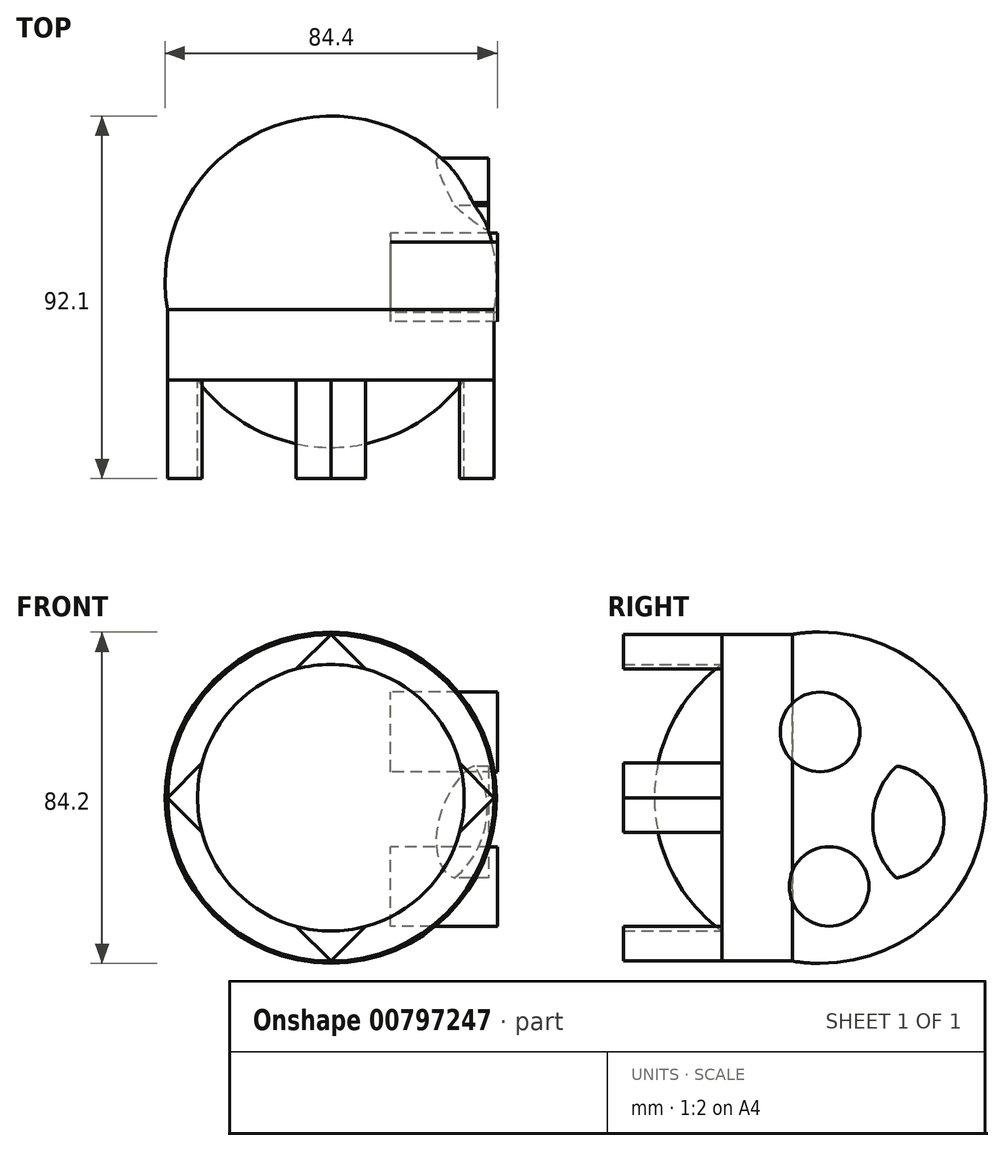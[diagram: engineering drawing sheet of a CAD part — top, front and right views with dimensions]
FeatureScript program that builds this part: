
annotation { "Feature Type Name" : "Feature", "Feature Type Description" : "" }
export const myFeature = defineFeature(function(context is Context, id is Id, definition is map)
    precondition{}
    {
        {
            var Q0;
            Q0=qCreatedBy(makeId("Front.planeOp"),FACE);
            var sketch = newSketch(context, id + "F0", { "sketchPlane" : qUnion([Q0])});
            skArc(sketch, "E0", {"start": v(0, 42.1) * mm, "mid": v(-42.1, 0) * mm, "end": v(0, -42.1) * mm});
            skLineSegment(sketch, "E1", {"start": v(0, 42.1) * mm, "end": v(0, -42.1) * mm});
            skSolve(sketch);
        }
        {
            var Q0;
            Q0 = qSketchRegion(id + "F0", true);
            var Q1;
            Q1=sQuery(id+"F0.wireOp",EDGE,"E1");
            revolve(context, id + "F1", {"surfaceOperationType" : NewSurfaceOperationType.NEW, "entities" : qUnion([Q0]), "axis" : qUnion([Q1]), "revolveType" : RevolveType.FULL});
        }
        {
            var Q0;
            Q0=qCreatedBy(makeId("Front.planeOp"),FACE);
            var sketch = newSketch(context, id + "F2", { "sketchPlane" : qUnion([Q0])});
            skCircle(sketch, "E2", {"center": v(0, 0) * mm, "radius": 41.5 * mm});
            skSolve(sketch);
        }
        {
            var Q0;
            Q0 = qSketchRegion(id + "F2", true);
            extrude(context, id + "F3", {"entities" : qUnion([Q0]), "operationType" : NewBodyOperationType.ADD, "depth" : 25 * mm, "offsetDistance" : 25 * mm});
        }
        {
            var Q0;
            Q0=makeQuery(id+"F3.opExtrude","CAP_FACE",FACE,{"disambiguationData":[OSD([sQuery(id+"F2.wireOp",EDGE,"E2")])],"isStart":false});
            var sketch = newSketch(context, id + "F4", { "sketchPlane" : qUnion([Q0])});
            skLineSegment(sketch, "E3", {"start": v(41.5, 0) * mm, "end": v(-41.5, 0) * mm});
            skLineSegment(sketch, "E4", {"start": v(-41.5, 0) * mm, "end": v(0, 41.5) * mm});
            skLineSegment(sketch, "E5", {"start": v(0, 41.5) * mm, "end": v(41.5, 0) * mm});
            skLineSegment(sketch, "E6", {"start": v(41.5, 0) * mm, "end": v(0, -41.5) * mm});
            skLineSegment(sketch, "E7", {"start": v(0, -41.5) * mm, "end": v(-41.5, 0) * mm});
            skSolve(sketch);
        }
        {
            var Q0;
            {var subQ0=sQuery(id+"F4.wireOp",EDGE,"E5");var subQ1=sQuery(id+"F4.wireOp",EDGE,"E4");var subQ2=sQuery(id+"F2.wireOp",EDGE,"E2");var subQ3=makeQuery(id+"F4.imprint","INTERSECT",VERTEX,{"derivedFrom":[makeQuery(id+"F3.opExtrude","CAP_EDGE",EDGE,{"disambiguationData":[OSD([subQ2])],"isStart":false}),subQ1,subQ0]});Q0=makeQuery(id+"F4.imprint","IMPRINT",FACE,{"disambiguationData":[TD([[makeQuery(id+"F4.imprint","IMPRINT",EDGE,{"disambiguationData":[TD([[subQ3,1.0]])],"derivedFrom":subQ1}),-1.0]])]});}
            var Q1;
            {var subQ1=sQuery(id+"F4.wireOp",EDGE,"E3");var subQ2=sQuery(id+"F2.wireOp",EDGE,"E2");var subQ4=makeQuery(id+"F3.boolean.opBoolean","INTERSECT",EDGE,{"derivedFrom":[makeQuery(id+"F1.opRevolve","SWEPT_FACE",FACE,{"disambiguationData":[OSD([sQuery(id+"F0.wireOp",EDGE,"E0")])]}),makeQuery(id+"F3.opExtrude","CAP_FACE",FACE,{"disambiguationData":[OSD([subQ2])],"isStart":false})]});var subQ5=makeQuery(id+"F4.imprint","INTERSECT",VERTEX,{"disambiguationData":[OD(0.0)],"derivedFrom":[subQ4,subQ1]});Q1=makeQuery(id+"F4.imprint","IMPRINT",FACE,{"disambiguationData":[TD([[makeQuery(id+"F4.imprint","IMPRINT",EDGE,{"disambiguationData":[TD([[subQ5,1.0]])],"derivedFrom":subQ1}),-1.0]])]});}
            var Q2;
            {var subQ1=sQuery(id+"F4.wireOp",EDGE,"E3");var subQ2=sQuery(id+"F2.wireOp",EDGE,"E2");var subQ4=makeQuery(id+"F3.boolean.opBoolean","INTERSECT",EDGE,{"derivedFrom":[makeQuery(id+"F1.opRevolve","SWEPT_FACE",FACE,{"disambiguationData":[OSD([sQuery(id+"F0.wireOp",EDGE,"E0")])]}),makeQuery(id+"F3.opExtrude","CAP_FACE",FACE,{"disambiguationData":[OSD([subQ2])],"isStart":false})]});var subQ5=makeQuery(id+"F4.imprint","INTERSECT",VERTEX,{"disambiguationData":[OD(0.0)],"derivedFrom":[subQ4,subQ1]});Q2=makeQuery(id+"F4.imprint","IMPRINT",FACE,{"disambiguationData":[TD([[makeQuery(id+"F4.imprint","IMPRINT",EDGE,{"disambiguationData":[TD([[subQ5,1.0]])],"derivedFrom":subQ1}),1.0]])]});}
            var Q3;
            {var subQ0=sQuery(id+"F4.wireOp",EDGE,"E7");var subQ1=sQuery(id+"F4.wireOp",EDGE,"E6");var subQ2=sQuery(id+"F2.wireOp",EDGE,"E2");var subQ3=makeQuery(id+"F4.imprint","INTERSECT",VERTEX,{"derivedFrom":[makeQuery(id+"F3.opExtrude","CAP_EDGE",EDGE,{"disambiguationData":[OSD([subQ2])],"isStart":false}),subQ1,subQ0]});Q3=makeQuery(id+"F4.imprint","IMPRINT",FACE,{"disambiguationData":[TD([[makeQuery(id+"F4.imprint","IMPRINT",EDGE,{"disambiguationData":[TD([[subQ3,1.0]])],"derivedFrom":subQ1}),-1.0]])]});}
            var Q4;
            {var subQ1=sQuery(id+"F4.wireOp",EDGE,"E3");var subQ2=sQuery(id+"F2.wireOp",EDGE,"E2");var subQ4=makeQuery(id+"F3.boolean.opBoolean","INTERSECT",EDGE,{"derivedFrom":[makeQuery(id+"F1.opRevolve","SWEPT_FACE",FACE,{"disambiguationData":[OSD([sQuery(id+"F0.wireOp",EDGE,"E0")])]}),makeQuery(id+"F3.opExtrude","CAP_FACE",FACE,{"disambiguationData":[OSD([subQ2])],"isStart":false})]});var subQ5=makeQuery(id+"F4.imprint","INTERSECT",VERTEX,{"disambiguationData":[OD(1.0)],"derivedFrom":[subQ4,subQ1]});Q4=makeQuery(id+"F4.imprint","IMPRINT",FACE,{"disambiguationData":[TD([[makeQuery(id+"F4.imprint","IMPRINT",EDGE,{"disambiguationData":[TD([[subQ5,-1.0]])],"derivedFrom":subQ1}),1.0]])]});}
            var Q5;
            {var subQ1=sQuery(id+"F4.wireOp",EDGE,"E3");var subQ2=sQuery(id+"F2.wireOp",EDGE,"E2");var subQ4=makeQuery(id+"F3.boolean.opBoolean","INTERSECT",EDGE,{"derivedFrom":[makeQuery(id+"F1.opRevolve","SWEPT_FACE",FACE,{"disambiguationData":[OSD([sQuery(id+"F0.wireOp",EDGE,"E0")])]}),makeQuery(id+"F3.opExtrude","CAP_FACE",FACE,{"disambiguationData":[OSD([subQ2])],"isStart":false})]});var subQ5=makeQuery(id+"F4.imprint","INTERSECT",VERTEX,{"disambiguationData":[OD(1.0)],"derivedFrom":[subQ4,subQ1]});Q5=makeQuery(id+"F4.imprint","IMPRINT",FACE,{"disambiguationData":[TD([[makeQuery(id+"F4.imprint","IMPRINT",EDGE,{"disambiguationData":[TD([[subQ5,-1.0]])],"derivedFrom":subQ1}),-1.0]])]});}
            extrude(context, id + "F5", {"entities" : qUnion([Q0, Q1, Q2, Q3, Q4, Q5]), "operationType" : NewBodyOperationType.ADD, "depth" : 25 * mm, "offsetDistance" : 25 * mm});
        }
        {
            var Q0;
            Q0=qCreatedBy(makeId("Right.planeOp"),FACE);
            cPlane(context, id + "F6", {"entities" : qUnion([Q0]), "cplaneType" : CPlaneType.OFFSET, "offset" : 15.1 * mm, "width" : 150 * mm, "height" : 150 * mm});
        }
        {
            var Q0;
            Q0=qCreatedBy(id+"F6.planeOp",FACE);
            var sketch = newSketch(context, id + "F7", { "sketchPlane" : qUnion([Q0])});
            skCircle(sketch, "E8", {"center": v(0, 16.73) * mm, "radius": 10.13 * mm});
            skCircle(sketch, "E9", {"center": v(2.3, -22.54) * mm, "radius": 10.1 * mm});
            skSolve(sketch);
        }
        {
            var Q0;
            Q0 = qSketchRegion(id + "F7", true);
            extrude(context, id + "F8", {"entities" : qUnion([Q0]), "depth" : 27.2 * mm, "offsetDistance" : 25 * mm});
        }
        {
            var Q0;
            Q0=qCreatedBy(id+"F6.planeOp",FACE);
            var sketch = newSketch(context, id + "F9", { "sketchPlane" : qUnion([Q0])});
            skArc(sketch, "E10", {"start": v(19.34, -20.38) * mm, "mid": v(31.43, -6.5) * mm, "end": v(20.07, 7.96) * mm});
            skArc(sketch, "E11", {"start": v(19.34, 7.96) * mm, "mid": v(13.35, -6.2) * mm, "end": v(19.34, -20.38) * mm});
            skLineSegment(sketch, "E12", {"start": v(19.34, 7.96) * mm, "end": v(20.07, 7.96) * mm});
            skSolve(sketch);
        }
        {
            var Q0;
            Q0 = qSketchRegion(id + "F9", true);
            extrude(context, id + "F10", {"entities" : qUnion([Q0]), "operationType" : NewBodyOperationType.ADD, "depth" : 25 * mm, "offsetDistance" : 25 * mm});
        }
    });
